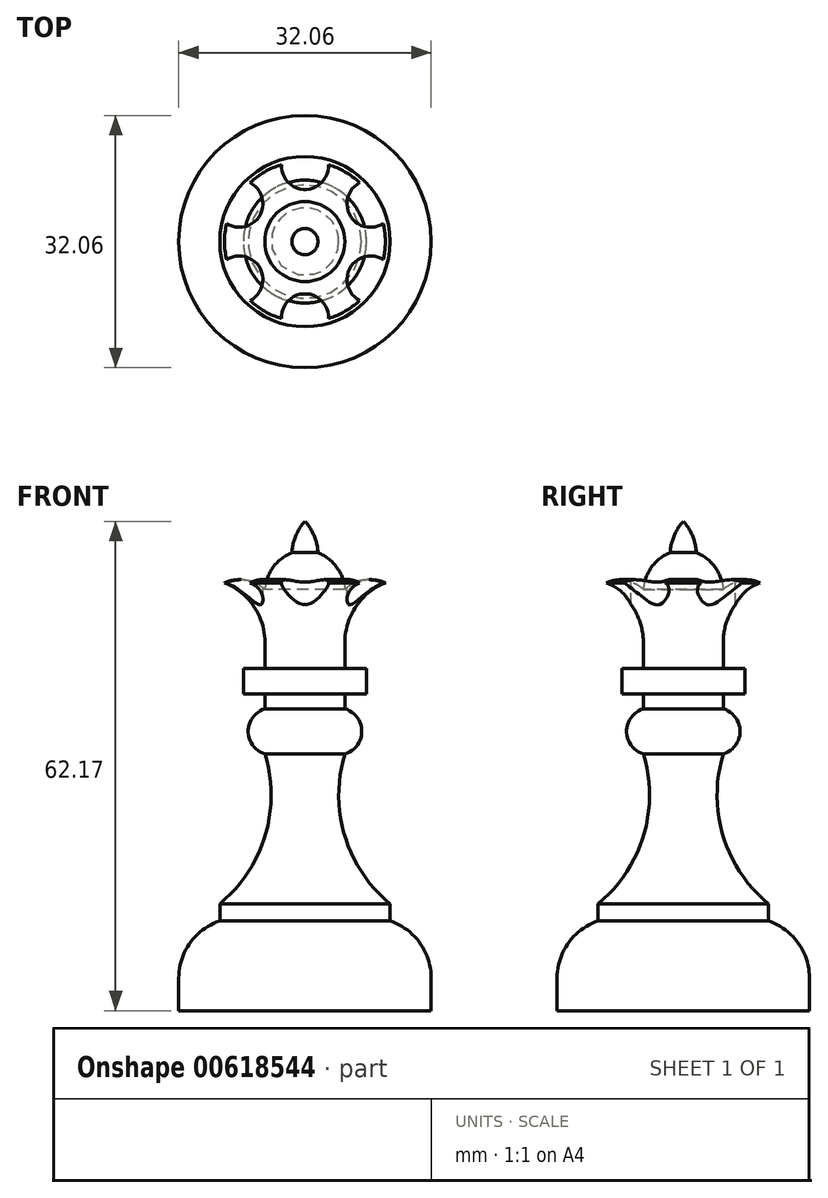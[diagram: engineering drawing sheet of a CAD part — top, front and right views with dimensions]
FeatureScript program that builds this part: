
annotation { "Feature Type Name" : "Feature", "Feature Type Description" : "" }
export const myFeature = defineFeature(function(context is Context, id is Id, definition is map)
    precondition{}
    {
        {
            var Q0;
            Q0=qCreatedBy(makeId("Front.planeOp"),FACE);
            var sketch = newSketch(context, id + "F0", { "sketchPlane" : qUnion([Q0])});
            skLineSegment(sketch, "E0", {"start": v(0, 0) * mm, "end": v(16.03, 0) * mm});
            skLineSegment(sketch, "E1", {"start": v(16.03, 4.15) * mm, "end": v(16.03, 0) * mm});
            skArc(sketch, "E2", {"start": v(16.03, 4.15) * mm, "mid": v(14.59, 8.62) * mm, "end": v(10.8, 11.4) * mm});
            skLineSegment(sketch, "E3", {"start": v(10.8, 11.4) * mm, "end": v(10.8, 13.59) * mm});
            skArc(sketch, "E4", {"start": v(5.08, 32.62) * mm, "mid": v(5.05, 22.23) * mm, "end": v(10.8, 13.59) * mm});
            skArc(sketch, "E5", {"start": v(5.08, 32.62) * mm, "mid": v(7.21, 35.49) * mm, "end": v(5.08, 38.35) * mm});
            skLineSegment(sketch, "E6", {"start": v(5.08, 38.35) * mm, "end": v(5.08, 40.2) * mm});
            skLineSegment(sketch, "E7", {"start": v(5.08, 43.5) * mm, "end": v(5.08, 46.78) * mm});
            skArc(sketch, "E8", {"start": v(10.22, 54.36) * mm, "mid": v(6.48, 51.36) * mm, "end": v(5.08, 46.78) * mm});
            skArc(sketch, "E9", {"start": v(5.08, 53.52) * mm, "mid": v(4.04, 56.34) * mm, "end": v(1.66, 58.19) * mm});
            skArc(sketch, "E10", {"start": v(10.22, 54.36) * mm, "mid": v(7.53, 54.69) * mm, "end": v(5.08, 53.52) * mm});
            skArc(sketch, "E11", {"start": v(1.66, 58.19) * mm, "mid": v(1.17, 60.32) * mm, "end": v(0, 62.17) * mm});
            skPoint(sketch, "E12.orphan", {"position": v(0, 58.57) * mm});
            skLineSegment(sketch, "E13", {"start": v(0, 62.17) * mm, "end": v(0, 0) * mm});
            skLineSegment(sketch, "E14", {"start": v(5.08, 40.2) * mm, "end": v(7.81, 40.2) * mm});
            skLineSegment(sketch, "E15", {"start": v(7.81, 40.2) * mm, "end": v(7.81, 43.5) * mm});
            skPoint(sketch, "E15.endSnap0", {"position": v(5.08, 43.5) * mm});
            skLineSegment(sketch, "E16", {"start": v(7.81, 43.5) * mm, "end": v(5.08, 43.5) * mm});
            skSolve(sketch);
        }
        {
            var Q0;
            Q0=makeQuery(id+"F0.imprint","IMPRINT",FACE,{"disambiguationData":[TD([[makeQuery(id+"F0.imprint","IMPRINT",EDGE,{"derivedFrom":sQuery(id+"F0.wireOp",EDGE,"E0")}),1.0]])]});
            var Q1;
            Q1=sQuery(id+"F0.wireOp",EDGE,"E13");
            revolve(context, id + "F1", {"entities" : qUnion([Q0]), "axis" : qUnion([Q1]), "revolveType" : RevolveType.FULL});
        }
        {
            var Q0;
            Q0=qCreatedBy(makeId("Top.planeOp"),FACE);
            cPlane(context, id + "F2", {"entities" : qUnion([Q0]), "cplaneType" : CPlaneType.OFFSET, "offset" : 54.7 * mm, "width" : 150 * mm, "height" : 150 * mm});
        }
        {
            var Q0;
            Q0=qCreatedBy(id+"F2.planeOp",FACE);
            var sketch = newSketch(context, id + "F3", { "sketchPlane" : qUnion([Q0])});
            skCircle(sketch, "E17", {"center": v(0, 9.63) * mm, "radius": 3 * mm});
            skCircle(sketch, "E18.1.0", {"center": v(-8.34, 4.81) * mm, "radius": 3 * mm});
            skCircle(sketch, "E18.2.0", {"center": v(-8.34, -4.81) * mm, "radius": 3 * mm});
            skCircle(sketch, "E18.3.0", {"center": v(0, -9.63) * mm, "radius": 3 * mm});
            skCircle(sketch, "E18.4.0", {"center": v(8.34, -4.81) * mm, "radius": 3 * mm});
            skCircle(sketch, "E18.5.0", {"center": v(8.34, 4.81) * mm, "radius": 3 * mm});
            skPoint(sketch, "E18.center", {"position": v(0, 0) * mm});
            skSolve(sketch);
        }
        {
            var Q0;
            Q0=makeQuery(id+"F3.imprint","IMPRINT",FACE,{"disambiguationData":[TD([[makeQuery(id+"F3.imprint","IMPRINT",EDGE,{"derivedFrom":sQuery(id+"F3.wireOp",EDGE,"E18.1.0")}),1.0]])]});
            var Q1;
            Q1=makeQuery(id+"F3.imprint","IMPRINT",FACE,{"disambiguationData":[TD([[makeQuery(id+"F3.imprint","IMPRINT",EDGE,{"derivedFrom":sQuery(id+"F3.wireOp",EDGE,"E17")}),1.0]])]});
            var Q2;
            Q2=makeQuery(id+"F3.imprint","IMPRINT",FACE,{"disambiguationData":[TD([[makeQuery(id+"F3.imprint","IMPRINT",EDGE,{"derivedFrom":sQuery(id+"F3.wireOp",EDGE,"E18.5.0")}),1.0]])]});
            var Q3;
            Q3=makeQuery(id+"F3.imprint","IMPRINT",FACE,{"disambiguationData":[TD([[makeQuery(id+"F3.imprint","IMPRINT",EDGE,{"derivedFrom":sQuery(id+"F3.wireOp",EDGE,"E18.4.0")}),1.0]])]});
            var Q4;
            Q4=makeQuery(id+"F3.imprint","IMPRINT",FACE,{"disambiguationData":[TD([[makeQuery(id+"F3.imprint","IMPRINT",EDGE,{"derivedFrom":sQuery(id+"F3.wireOp",EDGE,"E18.3.0")}),1.0]])]});
            var Q5;
            Q5=makeQuery(id+"F3.imprint","IMPRINT",FACE,{"disambiguationData":[TD([[makeQuery(id+"F3.imprint","IMPRINT",EDGE,{"derivedFrom":sQuery(id+"F3.wireOp",EDGE,"E18.2.0")}),1.0]])]});
            extrude(context, id + "F4", {"entities" : qUnion([Q0, Q1, Q2, Q3, Q4, Q5]), "operationType" : NewBodyOperationType.REMOVE, "endBound" : BoundingType.SYMMETRIC, "oppositeDirection" : true, "depth" : 7 * mm, "offsetDistance" : 25 * mm});
        }
    });
